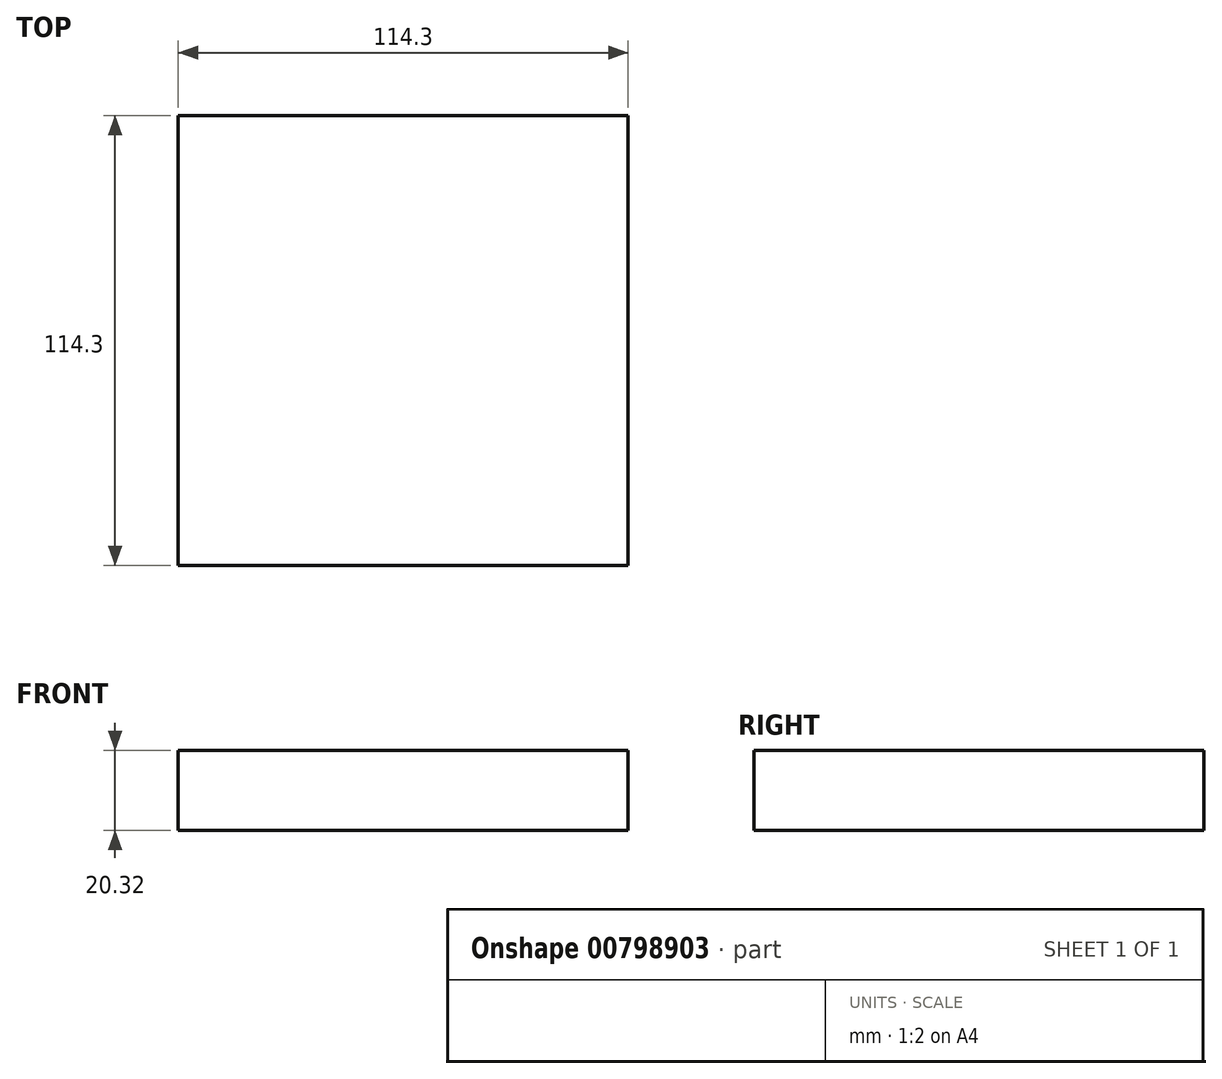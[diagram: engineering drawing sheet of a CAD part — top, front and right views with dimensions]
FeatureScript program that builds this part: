
annotation { "Feature Type Name" : "Feature", "Feature Type Description" : "" }
export const myFeature = defineFeature(function(context is Context, id is Id, definition is map)
    precondition{}
    {
        {
            var Q0;
            Q0=qCreatedBy(makeId("Top.planeOp"),FACE);
            var sketch = newSketch(context, id + "F0", { "sketchPlane" : qUnion([Q0])});
            skLineSegment(sketch, "E0.bottom", {"start": v(57.15, -57.15) * mm, "end": v(-57.15, -57.15) * mm});
            skLineSegment(sketch, "E0.top", {"start": v(57.15, 57.15) * mm, "end": v(-57.15, 57.15) * mm});
            skLineSegment(sketch, "E0.left", {"start": v(57.15, -57.15) * mm, "end": v(57.15, 57.15) * mm});
            skLineSegment(sketch, "E0.right", {"start": v(-57.15, -57.15) * mm, "end": v(-57.15, 57.15) * mm});
            skPoint(sketch, "E0.middle", {"position": v(0, 0) * mm});
            skSolve(sketch);
        }
        {
            var Q0;
            Q0=makeQuery(id+"F0.imprint","IMPRINT",FACE,{"disambiguationData":[TD([[makeQuery(id+"F0.imprint","IMPRINT",EDGE,{"derivedFrom":sQuery(id+"F0.wireOp",EDGE,"E0.bottom")}),-1.0]])]});
            extrude(context, id + "F1", {"entities" : qUnion([Q0]), "depth" : 20.32 * mm, "offsetDistance" : 25.4 * mm});
        }
    });
